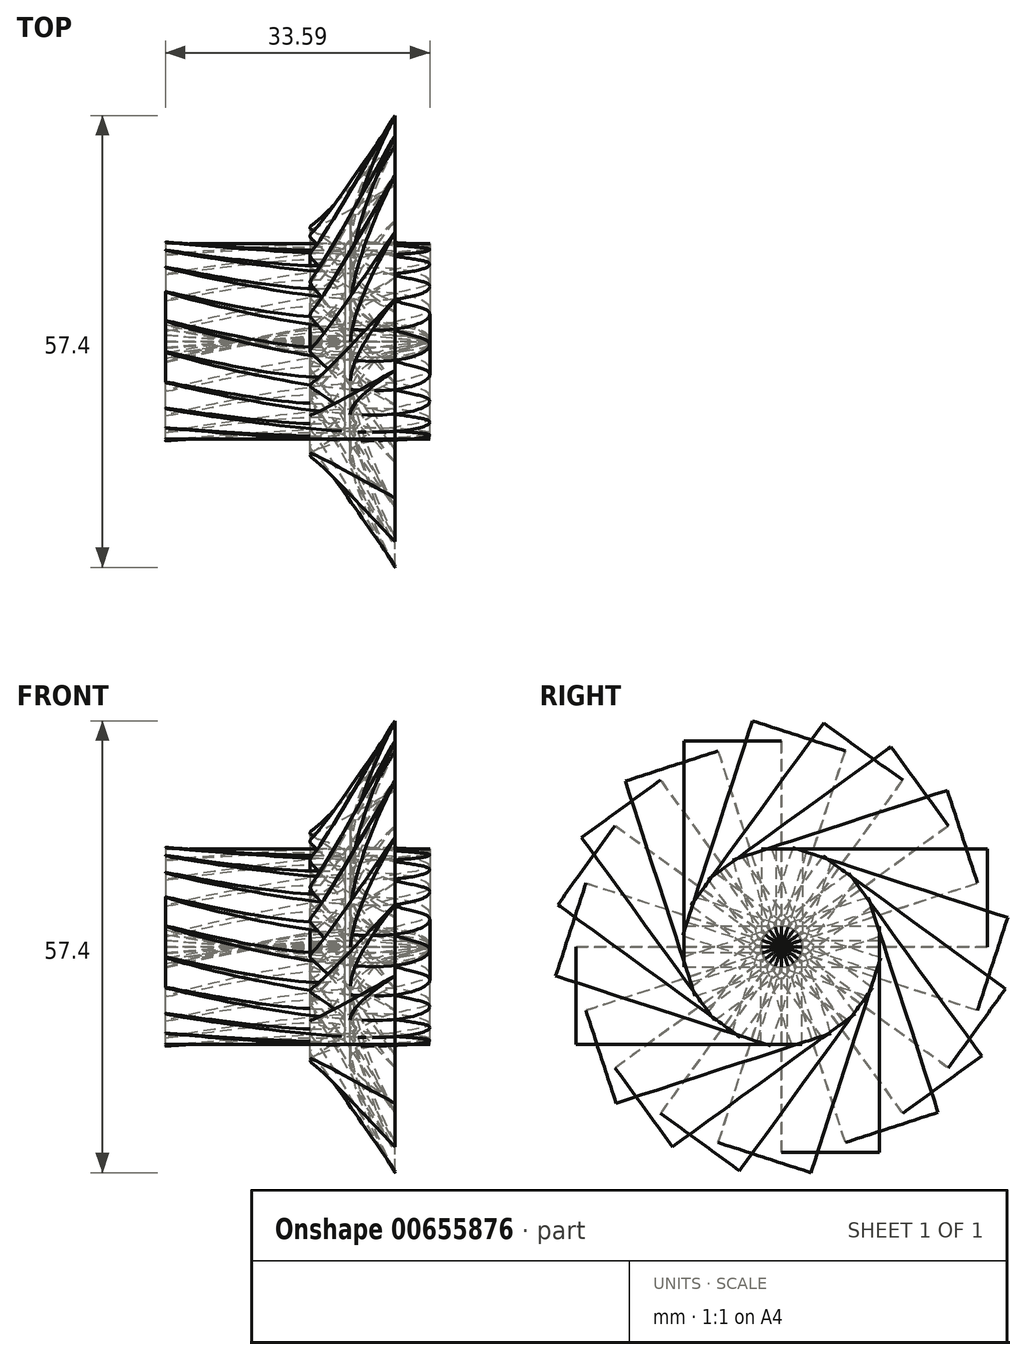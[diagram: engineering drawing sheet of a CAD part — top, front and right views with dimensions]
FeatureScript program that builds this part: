
annotation { "Feature Type Name" : "Feature", "Feature Type Description" : "" }
export const myFeature = defineFeature(function(context is Context, id is Id, definition is map)
    precondition{}
    {
        {
            var Q0;
            Q0=qCreatedBy(makeId("Top.planeOp"),FACE);
            var sketch = newSketch(context, id + "F0", { "sketchPlane" : qUnion([Q0])});
            skLineSegment(sketch, "E0.bottom", {"start": v(-33.88, 0) * mm, "end": v(35.47, 0) * mm});
            skLineSegment(sketch, "E0.top", {"start": v(-33.88, -19.05) * mm, "end": v(35.47, -19.05) * mm});
            skLineSegment(sketch, "E0.left", {"start": v(-33.88, 0) * mm, "end": v(-33.88, -19.05) * mm});
            skLineSegment(sketch, "E0.right", {"start": v(35.47, 0) * mm, "end": v(35.47, -19.05) * mm});
            skSolve(sketch);
        }
        {
            var Q0;
            Q0=qCreatedBy(makeId("Front.planeOp"),FACE);
            var sketch = newSketch(context, id + "F1", { "sketchPlane" : qUnion([Q0])});
            skFitSpline(sketch, "E1", {"points": [v(-29.06, 2.62) * mm, v(-6.62, 0) * mm, v(-10.6, 7.1) * mm, v(-10.2, 8.5) * mm, v(0, 26.15) * mm, v(-5.28, 5.47) * mm, v(4.22, 0) * mm, v(-2.06, -2.54) * mm, v(-29.06, 2.62) * mm]});
            skSolve(sketch);
        }
        {
            var Q0;
            Q0=makeQuery(id+"F1.imprint","IMPRINT",FACE,{"disambiguationData":[TD([[makeQuery(id+"F1.imprint","IMPRINT",EDGE,{"derivedFrom":sQuery(id+"F1.wireOp",EDGE,"E1")}),-1.0]])]});
            extrude(context, id + "F2", {"entities" : qUnion([Q0]), "depth" : 12.4 * mm, "offsetDistance" : 25 * mm});
        }
        {
            var Q0;
            Q0=makeQuery(id+"F2.opExtrude","SWEPT_BODY",BODY,{"disambiguationData":[OSD([sQuery(id+"F1.wireOp",EDGE,"E1")])]});
            var Q1;
            Q1=sQuery(id+"F0.wireOp",EDGE,"E0.bottom");
            circularPattern(context, id + "F3", {"entities" : qUnion([Q0]), "axis" : qUnion([Q1]), "angle" : 360 * degree, "instanceCount" : 20, "equalSpace" : true});
        }
    });
